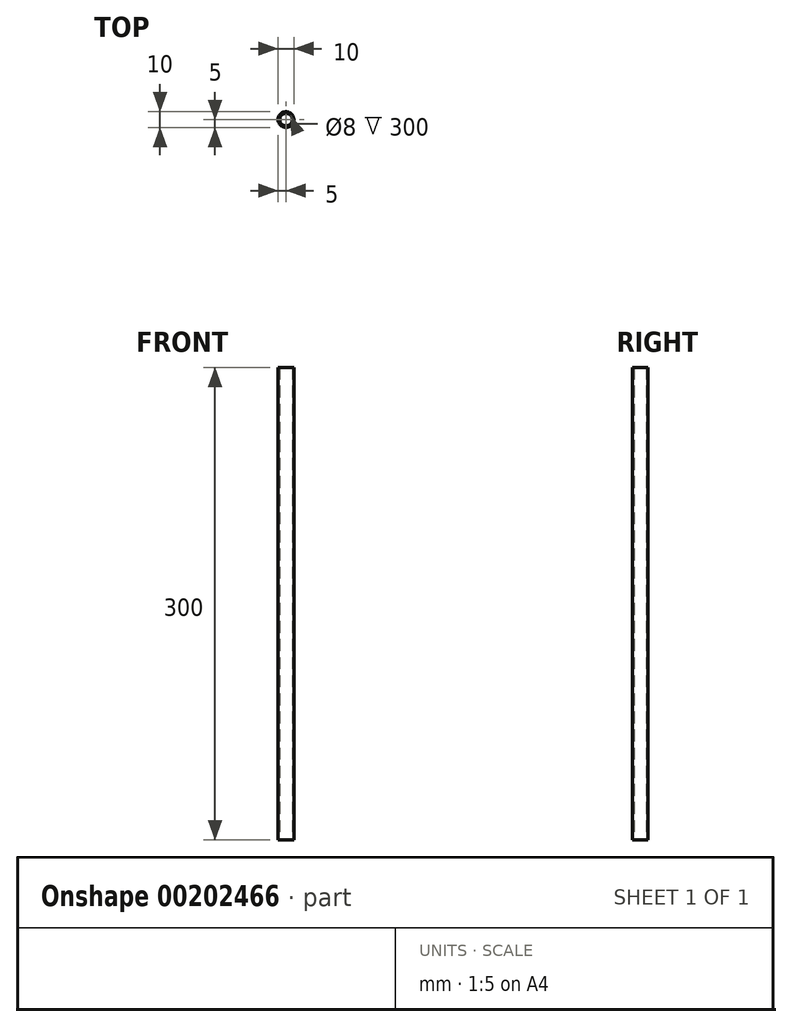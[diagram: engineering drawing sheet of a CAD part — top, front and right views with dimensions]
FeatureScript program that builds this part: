
annotation { "Feature Type Name" : "Feature", "Feature Type Description" : "" }
export const myFeature = defineFeature(function(context is Context, id is Id, definition is map)
    precondition{}
    {
        {
            var Q0;
            Q0=qCreatedBy(makeId("Top.planeOp"),FACE);
            var sketch = newSketch(context, id + "F0", { "sketchPlane" : qUnion([Q0])});
            skCircle(sketch, "E0", {"center": v(0, 0) * mm, "radius": 4 * mm});
            skCircle(sketch, "E1.0", {"center": v(0, 0) * mm, "radius": 5 * mm});
            skSolve(sketch);
        }
        {
            var Q0;
            Q0=qSketchRegion(id+"F0",true);
            extrude(context, id + "F1", {"entities" : qUnion([Q0]), "depth" : 300 * mm});
        }
    });
